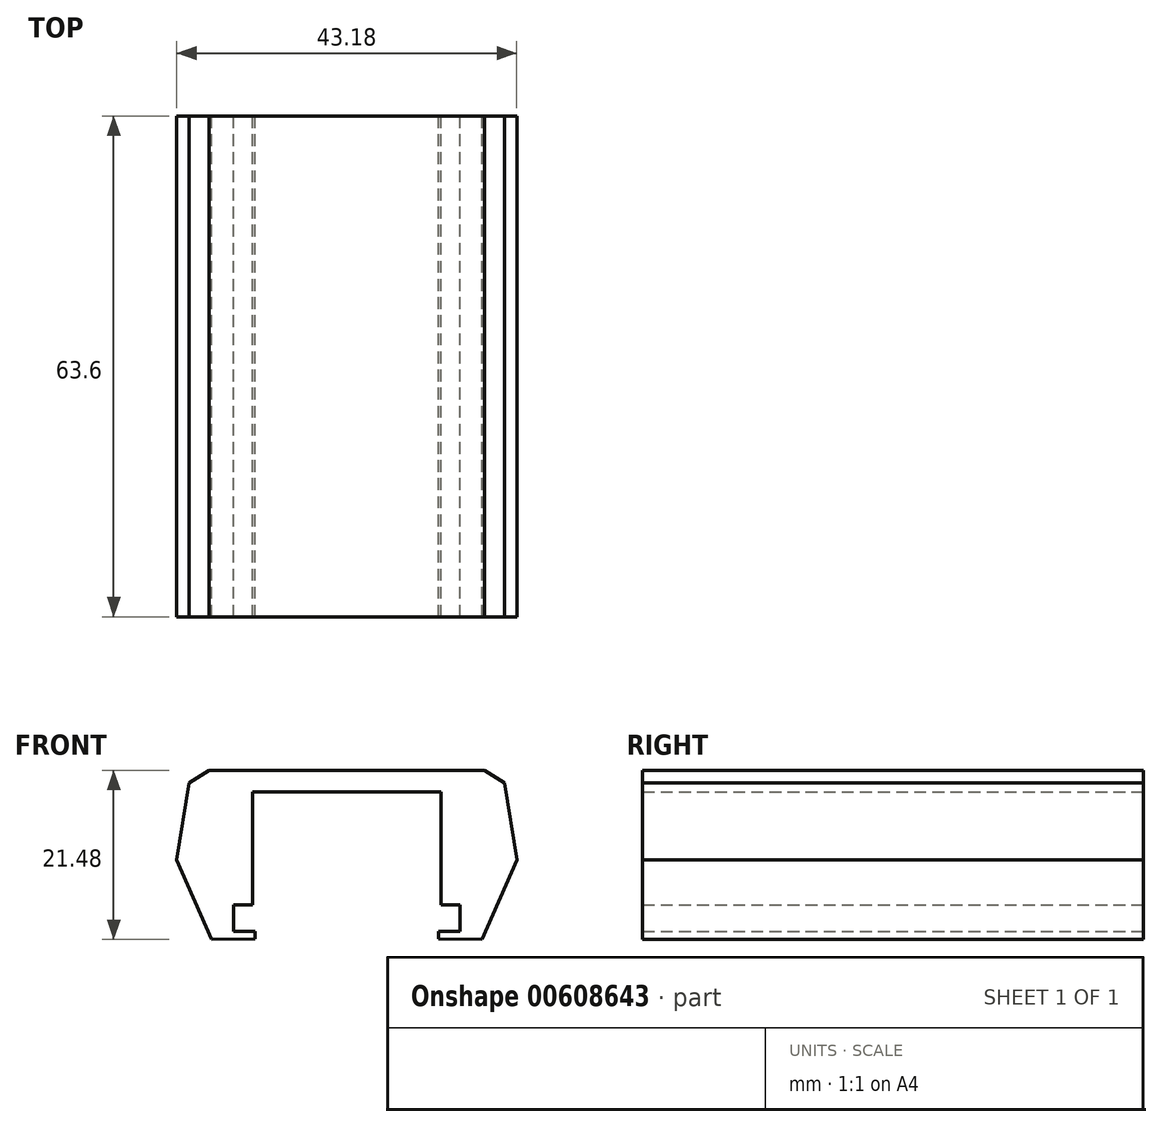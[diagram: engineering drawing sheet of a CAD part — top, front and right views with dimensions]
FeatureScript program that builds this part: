
annotation { "Feature Type Name" : "Feature", "Feature Type Description" : "" }
export const myFeature = defineFeature(function(context is Context, id is Id, definition is map)
    precondition{}
    {
        {
            var Q0;
            Q0=qCreatedBy(makeId("Front.planeOp"),FACE);
            var sketch = newSketch(context, id + "F0", { "sketchPlane" : qUnion([Q0])});
            skLineSegment(sketch, "E0", {"start": v(-11.64, 2.42) * mm, "end": v(-11.64, 3.35) * mm});
            skLineSegment(sketch, "E1", {"start": v(-11.64, 3.35) * mm, "end": v(-14.36, 3.35) * mm});
            skLineSegment(sketch, "E2", {"start": v(-14.36, 3.35) * mm, "end": v(-14.36, 6.75) * mm});
            skLineSegment(sketch, "E3", {"start": v(-11.94, 21.09) * mm, "end": v(0, 21.09) * mm});
            skLineSegment(sketch, "E4", {"start": v(0, 21.09) * mm, "end": v(0, 23.84) * mm});
            skLineSegment(sketch, "E5", {"start": v(0, 23.84) * mm, "end": v(-17.5, 23.84) * mm});
            skLineSegment(sketch, "E6", {"start": v(-17.18, 2.36) * mm, "end": v(-11.64, 2.42) * mm});
            skLineSegment(sketch, "E7", {"start": v(-14.36, 6.75) * mm, "end": v(-11.94, 6.75) * mm});
            skLineSegment(sketch, "E8", {"start": v(-11.94, 6.75) * mm, "end": v(-11.94, 21.09) * mm});
            skLineSegment(sketch, "E9.trimOffspring", {"start": v(-16.22, 10.11) * mm, "end": v(-16.22, 10.1) * mm});
            skLineSegment(sketch, "E10", {"start": v(-17.5, 23.84) * mm, "end": v(-20, 22.2) * mm});
            skLineSegment(sketch, "E11", {"start": v(-20, 22.2) * mm, "end": v(-21.6, 12.47) * mm});
            skLineSegment(sketch, "E12", {"start": v(-21.6, 12.47) * mm, "end": v(-17.18, 2.36) * mm});
            skSolve(sketch);
        }
        {
            var Q0;
            Q0=makeQuery(id+"F0.imprint","IMPRINT",FACE,{"disambiguationData":[TD([[makeQuery(id+"F0.imprint","IMPRINT",EDGE,{"derivedFrom":sQuery(id+"F0.wireOp",EDGE,"E0")}),1.0]])]});
            extrude(context, id + "F1", {"entities" : qUnion([Q0]), "endBound" : BoundingType.SYMMETRIC, "depth" : 63.6 * mm, "offsetDistance" : 25 * mm});
        }
        {
            var Q0;
            Q0=makeQuery(id+"F1.opExtrude","SWEPT_BODY",BODY,{"disambiguationData":[OSD([sQuery(id+"F0.wireOp",EDGE,"E0"),sQuery(id+"F0.wireOp",EDGE,"E1"),sQuery(id+"F0.wireOp",EDGE,"E2"),sQuery(id+"F0.wireOp",EDGE,"E3"),sQuery(id+"F0.wireOp",EDGE,"E4"),sQuery(id+"F0.wireOp",EDGE,"E5"),sQuery(id+"F0.wireOp",EDGE,"E6"),sQuery(id+"F0.wireOp",EDGE,"E7"),sQuery(id+"F0.wireOp",EDGE,"E8"),sQuery(id+"F0.wireOp",EDGE,"E10"),sQuery(id+"F0.wireOp",EDGE,"E11"),sQuery(id+"F0.wireOp",EDGE,"E12")])]});
            var Q1;
            Q1=qCreatedBy(makeId("Right.planeOp"),FACE);
            mirror(context, id + "F2", {"operationType" : NewBodyOperationType.ADD, "entities" : qUnion([Q0]), "mirrorPlane" : qUnion([Q1])});
        }
    });
